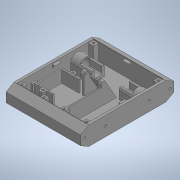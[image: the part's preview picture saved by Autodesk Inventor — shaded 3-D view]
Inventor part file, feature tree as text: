
AUTODESK INVENTOR PART (.ipt)
format: ipt  version: 2020 (Build 240168000, 168)  size: 722,944 bytes
history: native  units: in
note: dims shown in document units (in); Inventor stores cm internally (conversion verified against a paired STEP export)
features: extrude x21, sketch x21, projected_geometry x16, mirror x7, plane x1
ambient origin geometry x8: Origin, YZ Plane, XZ Plane, XY Plane, X Axis, Y Axis, Z Axis, Center Point
bodies: Solid1 (feature_tree)
feature tree (66):
  extrude  "Extrusion1"  Depth=5.9055in
  extrude  "Extrusion2"  TaperAngle=0.0deg  [1 undecoded]
  extrude  "Extrusion3"  Depth=1.063in
  extrude  "Extrusion4"  Depth=0.315in
  extrude  "Extrusion5"  TaperAngle=0.0deg  [1 undecoded]
  extrude  "Extrusion6"  Depth=0.5906in
  mirror  "Mirror1"
  extrude  "Extrusion7"  Depth=0.0787in
  mirror  "Mirror2"
  extrude  "Extrusion8"  Depth=0.6102in
  mirror  "Mirror3"
  plane  "Work Plane1"
  extrude  "Extrusion9"  Depth=0.7874in TaperAngle=0.0deg
  mirror  "Mirror4"
  extrude  "Extrusion10"  Depth=6.063in TaperAngle=0.0deg
  extrude  "Extrusion11"  Depth=0.1575in
  extrude  "Extrusion12"  TaperAngle=0.0deg  [1 undecoded]
  extrude  "Extrusion13"  Depth=0.2756in
  extrude  "Extrusion14"  Depth=0.4331in
  extrude  "Extrusion17"  Depth=2.7559in
  extrude  "Extrusion18"  Depth=0.0453in
  mirror  "Mirror6"
  extrude  "Extrusion19"  TaperAngle=0.0deg  [1 undecoded]
  mirror  "Mirror7"
  extrude  "Extrusion20"  Depth=0.0787in
  extrude  "Extrusion21"  Depth=0.993in
  extrude  "Extrusion22"  Depth=0.2756in
  extrude  "Extrusion23"  Depth=0.4724in
  mirror  "Mirror8"
  sketch  "Sketch1"  dims[d0=1.1811in d1=5.9055in]
  sketch  "Sketch2"  dims[d2=4.7244in d3=0.0in]
  projected_geometry  "Projected Loop1"
  sketch  "Sketch3"  dims[d4=0.1575in d5=1.063in]
  projected_geometry  "Projected Loop2"
  projected_geometry  "Projected Loop3"
  sketch  "Sketch4"  dims[d6=0.0in d8=0.315in]
  sketch  "Sketch5"  dims[d10=0.993in d11=0.0in]
  projected_geometry  "Projected Loop4"
  sketch  "Sketch6"  dims[d12=0.6496in d13=0.5906in]
  sketch  "Sketch7"  dims[d14=1.5748in d15=0.0787in]
  sketch  "Sketch9"  dims[d16=0.5512in d17=0.0in d18=0.6102in]
  sketch  "Sketch10"  dims[d19=0.4803in d20=0.7874in d21=0.0in]
  sketch  "Sketch12"  dims[d22=0.1654in d23=6.063in d24=0.0in]
  projected_geometry  "Projected Loop6"
  projected_geometry  "Projected Loop7"
  projected_geometry  "Projected Loop8"
  sketch  "Sketch13"  dims[d25=0.5114in d26=0.1575in]
  sketch  "Sketch14"  dims[d27=1.5748in d28=0.0in d29=0.0in]
  sketch  "Sketch15"  dims[d30=0.1575in d31=0.2756in]
  projected_geometry  "Projected Loop15"
  sketch  "Sketch16"  dims[d32=0.0in d33=0.4331in]
  projected_geometry  "Projected Loop19"
  projected_geometry  "Projected Loop20"
  projected_geometry  "Projected Loop21"
  projected_geometry  "Projected Loop22"
  projected_geometry  "Projected Loop23"
  projected_geometry  "Projected Loop24"
  sketch  "Sketch20"  dims[d34=0.0906in d38=2.7559in]
  sketch  "Sketch21"  dims[d40=0.0453in d41=0.0909in]
  sketch  "Sketch22"  dims[d42=0.2362in d43=0.0in]
  sketch  "Sketch23"  dims[d44=60.0deg d45=0.0787in]
  sketch  "Sketch25"  dims[d46=0.315in d48=0.993in]
  sketch  "Sketch26"  dims[d49=0.0in d53=0.2756in]
  projected_geometry  "Projected Loop25"
  sketch  "Sketch27"  dims[d54=0.0in d55=0.4724in d56=1.1811in d57=1.5748in d58=1.5748in d59=0.0787in d60=0.0787in d62=0.315in d63=0.7677in d64=0.0in d66=0.1476in d67=0.2756in d68=0.0in d69=0.7874in d70=0.2953in d71=0.1181in d72=0.0in d89=0.0157in d90=0.0157in d91=0.1476in d92=0.1476in d96=0.315in d97=0.1575in d98=0.1181in d99=0.0in d102=0.1772in d104=0.3346in d105=135.0deg d106=0.2362in d107=0.0in d108=0.0394in d109=0.0in d110=0.063in d111=0.0394in d112=0.0in d117=0.993in d118=0.063in d119=0.3937in d120=0.0in d121=45.0deg d122=0.993in d123=0.1969in d124=0.3937in d125=0.0in d126=45.0deg d127=0.1969in d128=0.993in d129=0.3937in d130=0.0in]
  projected_geometry  "Projected Loop26"
note: 4 required parameter values undecoded (feature->parameter linkage not recoverable at this tier; creation-order binding heuristic only, values carry confidence <= 0.55)
